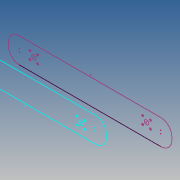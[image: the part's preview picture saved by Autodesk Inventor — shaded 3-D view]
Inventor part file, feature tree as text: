
AUTODESK INVENTOR PART (.ipt)
format: ipt  version: 2020 (Build 240168000, 168)  size: 115,200 bytes
history: native  units: mm
features: extrude x1, sketch x1
ambient origin geometry x8: Origin, YZ Plane, XZ Plane, XY Plane, X Axis, Y Axis, Z Axis, Center Point
bodies: Body1 (feature_tree)
feature tree (2):
  extrude  "Выдавливание4"  Depth=3.0mm TaperAngle=0.0deg
  sketch  "Эскиз4"
